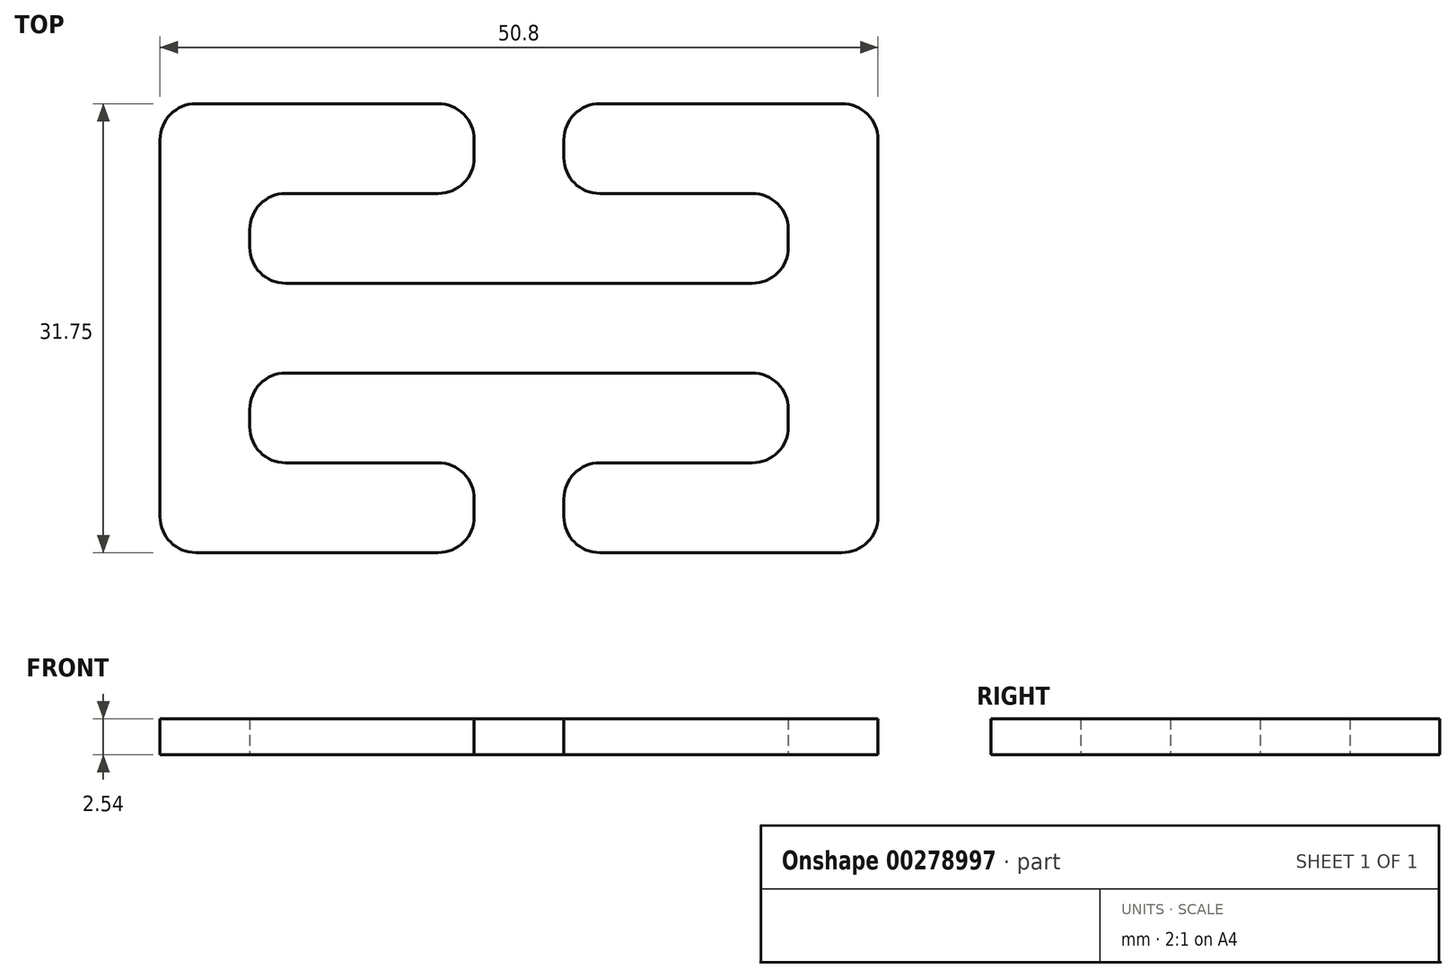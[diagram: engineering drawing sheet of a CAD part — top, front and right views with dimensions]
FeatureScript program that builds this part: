
annotation { "Feature Type Name" : "Feature", "Feature Type Description" : "" }
export const myFeature = defineFeature(function(context is Context, id is Id, definition is map)
    precondition{}
    {
        {
            var Q0;
            Q0=qCreatedBy(makeId("Top.planeOp"),FACE);
            var sketch = newSketch(context, id + "F0", { "sketchPlane" : qUnion([Q0])});
            skLineSegment(sketch, "E0", {"start": v(2.54, 95.25) * mm, "end": v(19.68, 95.25) * mm});
            skLineSegment(sketch, "E1", {"start": v(6.35, 86.36) * mm, "end": v(6.35, 85.1) * mm});
            skLineSegment(sketch, "E2", {"start": v(8.89, 82.55) * mm, "end": v(41.91, 82.55) * mm});
            skLineSegment(sketch, "E3", {"start": v(22.22, 92.71) * mm, "end": v(22.22, 91.44) * mm});
            skLineSegment(sketch, "E4", {"start": v(19.68, 88.9) * mm, "end": v(8.89, 88.9) * mm});
            skLineSegment(sketch, "E5", {"start": v(44.45, 85.1) * mm, "end": v(44.45, 86.36) * mm});
            skLineSegment(sketch, "E6", {"start": v(41.91, 88.9) * mm, "end": v(31.11, 88.9) * mm});
            skLineSegment(sketch, "E7", {"start": v(28.57, 91.44) * mm, "end": v(28.57, 92.71) * mm});
            skLineSegment(sketch, "E8", {"start": v(31.11, 95.25) * mm, "end": v(48.26, 95.25) * mm});
            skLineSegment(sketch, "E9", {"start": v(50.8, 92.71) * mm, "end": v(50.8, 66.04) * mm});
            skLineSegment(sketch, "E10", {"start": v(48.26, 63.5) * mm, "end": v(31.11, 63.5) * mm});
            skLineSegment(sketch, "E11", {"start": v(28.57, 66.04) * mm, "end": v(28.57, 67.31) * mm});
            skLineSegment(sketch, "E12", {"start": v(31.11, 69.85) * mm, "end": v(41.91, 69.85) * mm});
            skLineSegment(sketch, "E13", {"start": v(44.45, 72.4) * mm, "end": v(44.45, 73.66) * mm});
            skLineSegment(sketch, "E14", {"start": v(41.91, 76.2) * mm, "end": v(8.89, 76.2) * mm});
            skLineSegment(sketch, "E15", {"start": v(6.35, 73.66) * mm, "end": v(6.35, 72.4) * mm});
            skLineSegment(sketch, "E16", {"start": v(8.89, 69.85) * mm, "end": v(19.68, 69.85) * mm});
            skLineSegment(sketch, "E17", {"start": v(22.22, 67.31) * mm, "end": v(22.22, 66.04) * mm});
            skLineSegment(sketch, "E18", {"start": v(19.68, 63.5) * mm, "end": v(2.54, 63.5) * mm});
            skLineSegment(sketch, "E19", {"start": v(0, 92.71) * mm, "end": v(0, 66.04) * mm});
            skPoint(sketch, "E20.visualSharp", {"position": v(22.22, 95.25) * mm});
            skArc(sketch, "E20.filletArc", {"start": v(22.22, 92.71) * mm, "mid": v(21.48, 94.5) * mm, "end": v(19.68, 95.25) * mm});
            skPoint(sketch, "E21.visualSharp", {"position": v(22.22, 88.9) * mm});
            skArc(sketch, "E21.filletArc", {"start": v(19.68, 88.9) * mm, "mid": v(21.48, 89.64) * mm, "end": v(22.22, 91.44) * mm});
            skPoint(sketch, "E22.visualSharp", {"position": v(0, 95.25) * mm});
            skArc(sketch, "E22.filletArc", {"start": v(2.54, 95.25) * mm, "mid": v(0.74, 94.5) * mm, "end": v(0, 92.71) * mm});
            skPoint(sketch, "E23.visualSharp", {"position": v(0, 63.5) * mm});
            skArc(sketch, "E23.filletArc", {"start": v(0, 66.04) * mm, "mid": v(0.74, 64.24) * mm, "end": v(2.54, 63.5) * mm});
            skPoint(sketch, "E24.visualSharp", {"position": v(22.22, 63.5) * mm});
            skArc(sketch, "E24.filletArc", {"start": v(19.68, 63.5) * mm, "mid": v(21.48, 64.24) * mm, "end": v(22.22, 66.04) * mm});
            skPoint(sketch, "E25.visualSharp", {"position": v(22.22, 69.85) * mm});
            skArc(sketch, "E25.filletArc", {"start": v(22.22, 67.31) * mm, "mid": v(21.48, 69.1) * mm, "end": v(19.68, 69.85) * mm});
            skPoint(sketch, "E26.visualSharp", {"position": v(6.35, 69.85) * mm});
            skArc(sketch, "E26.filletArc", {"start": v(6.35, 72.4) * mm, "mid": v(7.1, 70.6) * mm, "end": v(8.89, 69.85) * mm});
            skPoint(sketch, "E27.visualSharp", {"position": v(6.35, 76.2) * mm});
            skArc(sketch, "E27.filletArc", {"start": v(8.89, 76.2) * mm, "mid": v(7.1, 75.46) * mm, "end": v(6.35, 73.66) * mm});
            skPoint(sketch, "E28.visualSharp", {"position": v(44.45, 76.2) * mm});
            skArc(sketch, "E28.filletArc", {"start": v(44.45, 73.66) * mm, "mid": v(43.7, 75.46) * mm, "end": v(41.91, 76.2) * mm});
            skPoint(sketch, "E29.visualSharp", {"position": v(44.45, 69.85) * mm});
            skArc(sketch, "E29.filletArc", {"start": v(41.91, 69.85) * mm, "mid": v(43.7, 70.6) * mm, "end": v(44.45, 72.4) * mm});
            skPoint(sketch, "E30.visualSharp", {"position": v(28.57, 69.85) * mm});
            skArc(sketch, "E30.filletArc", {"start": v(31.11, 69.85) * mm, "mid": v(29.32, 69.1) * mm, "end": v(28.57, 67.31) * mm});
            skPoint(sketch, "E31.visualSharp", {"position": v(28.57, 63.5) * mm});
            skArc(sketch, "E31.filletArc", {"start": v(28.57, 66.04) * mm, "mid": v(29.32, 64.24) * mm, "end": v(31.11, 63.5) * mm});
            skPoint(sketch, "E32.visualSharp", {"position": v(50.8, 63.5) * mm});
            skArc(sketch, "E32.filletArc", {"start": v(48.26, 63.5) * mm, "mid": v(50.06, 64.24) * mm, "end": v(50.8, 66.04) * mm});
            skPoint(sketch, "E33.visualSharp", {"position": v(50.8, 95.25) * mm});
            skArc(sketch, "E33.filletArc", {"start": v(50.8, 92.71) * mm, "mid": v(50.06, 94.5) * mm, "end": v(48.26, 95.25) * mm});
            skPoint(sketch, "E34.visualSharp", {"position": v(28.57, 95.25) * mm});
            skArc(sketch, "E34.filletArc", {"start": v(31.11, 95.25) * mm, "mid": v(29.32, 94.5) * mm, "end": v(28.57, 92.71) * mm});
            skPoint(sketch, "E35.visualSharp", {"position": v(28.57, 88.9) * mm});
            skArc(sketch, "E35.filletArc", {"start": v(28.57, 91.44) * mm, "mid": v(29.32, 89.64) * mm, "end": v(31.11, 88.9) * mm});
            skPoint(sketch, "E36.visualSharp", {"position": v(44.45, 88.9) * mm});
            skArc(sketch, "E36.filletArc", {"start": v(44.45, 86.36) * mm, "mid": v(43.7, 88.16) * mm, "end": v(41.91, 88.9) * mm});
            skPoint(sketch, "E37.visualSharp", {"position": v(44.45, 82.55) * mm});
            skArc(sketch, "E37.filletArc", {"start": v(41.91, 82.55) * mm, "mid": v(43.7, 83.3) * mm, "end": v(44.45, 85.1) * mm});
            skPoint(sketch, "E38.visualSharp", {"position": v(6.35, 82.55) * mm});
            skArc(sketch, "E38.filletArc", {"start": v(6.35, 85.1) * mm, "mid": v(7.1, 83.3) * mm, "end": v(8.89, 82.55) * mm});
            skPoint(sketch, "E39.visualSharp", {"position": v(6.35, 88.9) * mm});
            skArc(sketch, "E39.filletArc", {"start": v(8.89, 88.9) * mm, "mid": v(7.1, 88.16) * mm, "end": v(6.35, 86.36) * mm});
            skSolve(sketch);
        }
        {
            var Q0;
            Q0=makeQuery(id+"F0.imprint","IMPRINT",FACE,{"disambiguationData":[TD([[makeQuery(id+"F0.imprint","IMPRINT",EDGE,{"derivedFrom":sQuery(id+"F0.wireOp",EDGE,"E0")}),-1.0]])]});
            extrude(context, id + "F1", {"entities" : qUnion([Q0]), "depth" : 2.54 * mm});
        }
    });
